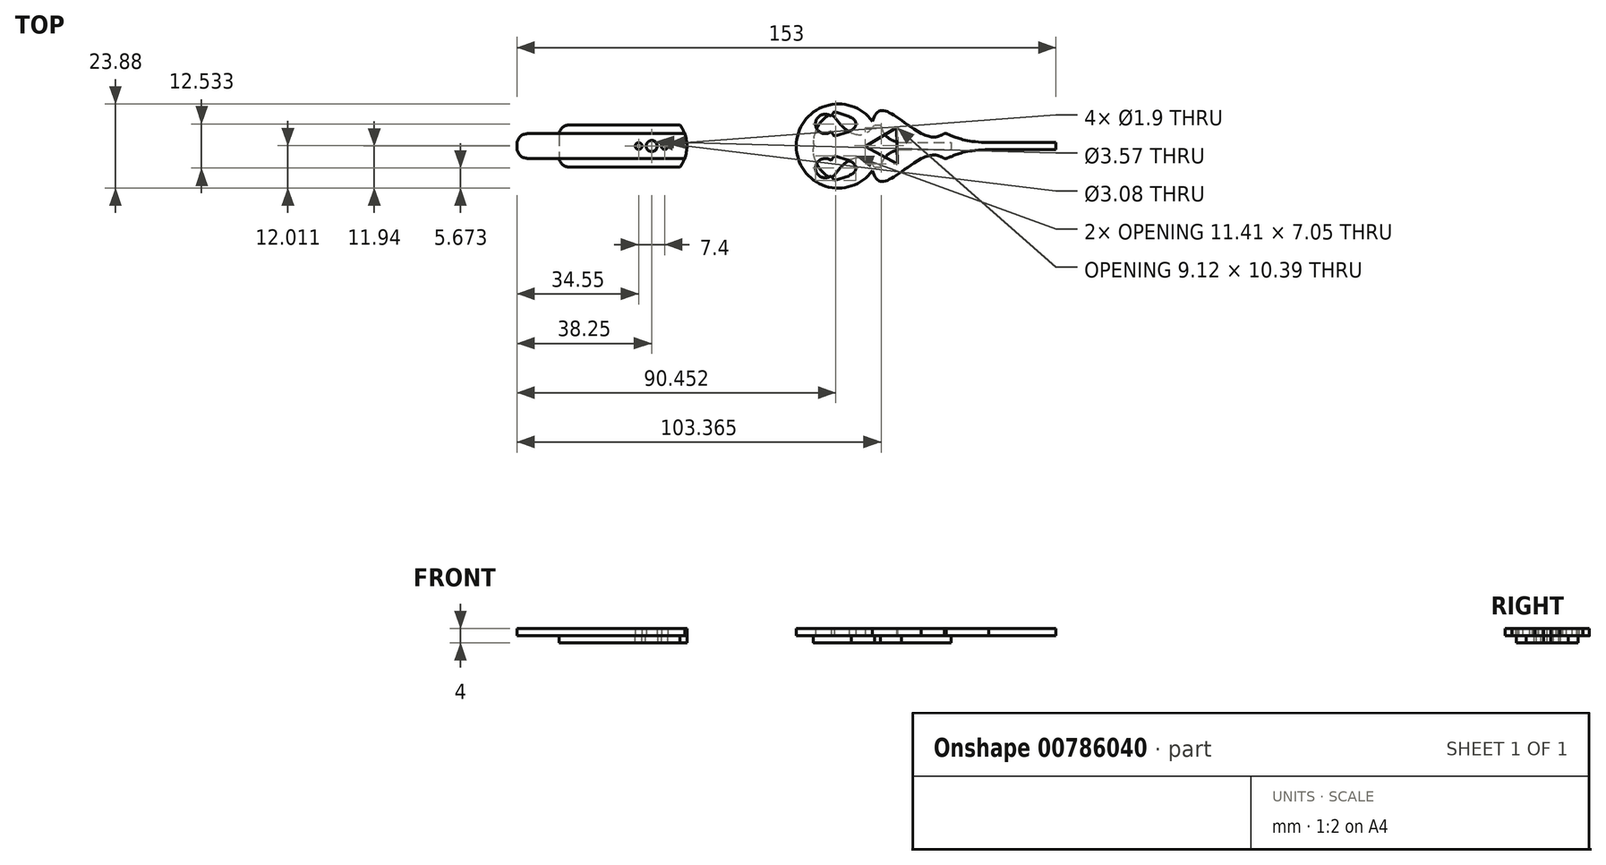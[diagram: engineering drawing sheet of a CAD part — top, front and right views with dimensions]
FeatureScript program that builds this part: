
annotation { "Feature Type Name" : "Feature", "Feature Type Description" : "" }
export const myFeature = defineFeature(function(context is Context, id is Id, definition is map)
    precondition{}
    {
        {
            var Q0;
            Q0=qCreatedBy(makeId("Top.planeOp"),FACE);
            var sketch = newSketch(context, id + "F0", { "sketchPlane" : qUnion([Q0])});
            skCircle(sketch, "E0", {"center": v(0, 0) * mm, "radius": 1.54 * mm});
            skLineSegment(sketch, "E1.bottom", {"start": v(-38.25, 3.5) * mm, "end": v(114.75, 3.5) * mm});
            skLineSegment(sketch, "E1.top", {"start": v(-38.25, -3.5) * mm, "end": v(114.75, -3.5) * mm});
            skLineSegment(sketch, "E1.left", {"start": v(-38.25, 3.5) * mm, "end": v(-38.25, -3.5) * mm});
            skLineSegment(sketch, "E1.right", {"start": v(114.75, 3.5) * mm, "end": v(114.75, -3.5) * mm});
            skCircle(sketch, "E2", {"center": v(0, 0) * mm, "radius": 10 * mm});
            skFitSpline(sketch, "E3", {"points": [v(76.5, -3.5) * mm, v(83.1, -3.5) * mm, v(95.63, -1) * mm], "startDerivative": vector(32.58, 14.52) * mm, "endDerivative": vector(48.68, 0.82) * mm});
            skFitSpline(sketch, "E4", {"points": [v(76.5, -3.5) * mm, v(64.41, -9.82) * mm, v(62.16, 0) * mm], "startDerivative": vector(-33.87, -20.38) * mm, "endDerivative": vector(3.66, 22.72) * mm});
            skLineSegment(sketch, "E5", {"start": v(0, 0) * mm, "end": v(229.5, 0) * mm, "construction": true});
            skLineSegment(sketch, "E6", {"start": v(95.63, -1) * mm, "end": v(114.75, -1) * mm});
            skFitSpline(sketch, "E7.MirrorCS", {"points": [v(76.5, 3.5) * mm, v(64.41, 9.82) * mm, v(62.16, 0) * mm], "startDerivative": vector(-33.87, 20.38) * mm, "endDerivative": vector(3.66, -22.72) * mm});
            skFitSpline(sketch, "E8.MirrorCS", {"points": [v(76.5, 3.5) * mm, v(83.1, 3.5) * mm, v(95.63, 1) * mm], "startDerivative": vector(32.58, -14.52) * mm, "endDerivative": vector(48.68, -0.82) * mm});
            skLineSegment(sketch, "E9.MirrorCS", {"start": v(95.63, 1) * mm, "end": v(114.75, 1) * mm});
            skCircle(sketch, "E10", {"center": v(52.97, 0) * mm, "radius": 11.94 * mm});
            skCircle(sketch, "E11.cCircle", {"center": v(52.97, 6.27) * mm, "radius": 3 * mm, "construction": true});
            skLineSegment(sketch, "E11.0", {"start": v(55.97, 8.45) * mm, "end": v(55.97, 4.09) * mm});
            skLineSegment(sketch, "E11.1", {"start": v(55.97, 4.09) * mm, "end": v(51.82, 2.74) * mm});
            skLineSegment(sketch, "E11.2", {"start": v(51.82, 2.74) * mm, "end": v(49.26, 6.27) * mm});
            skLineSegment(sketch, "E11.3", {"start": v(49.26, 6.27) * mm, "end": v(51.82, 9.8) * mm});
            skLineSegment(sketch, "E11.4", {"start": v(51.82, 9.8) * mm, "end": v(55.97, 8.45) * mm});
            skPoint(sketch, "E11.0.midPoint", {"position": v(55.97, 6.27) * mm});
            skCircle(sketch, "E12.MirrorC", {"center": v(52.97, -6.27) * mm, "radius": 3 * mm, "construction": true});
            skLineSegment(sketch, "E13.MirrorCS", {"start": v(51.82, -2.74) * mm, "end": v(49.26, -6.27) * mm});
            skLineSegment(sketch, "E14.MirrorCS", {"start": v(55.97, -4.09) * mm, "end": v(51.82, -2.74) * mm});
            skLineSegment(sketch, "E15.MirrorCS", {"start": v(55.97, -8.45) * mm, "end": v(55.97, -4.09) * mm});
            skLineSegment(sketch, "E16.MirrorCS", {"start": v(51.82, -9.8) * mm, "end": v(55.97, -8.45) * mm});
            skLineSegment(sketch, "E17.MirrorCS", {"start": v(49.26, -6.27) * mm, "end": v(51.82, -9.8) * mm});
            skCircle(sketch, "E18", {"center": v(49.26, 6.27) * mm, "radius": 2.76 * mm});
            skCircle(sketch, "E19.MirrorC", {"center": v(49.26, -6.27) * mm, "radius": 2.76 * mm});
            skCircle(sketch, "E20", {"center": v(55.97, 6.27) * mm, "radius": 1.94 * mm});
            skCircle(sketch, "E21.MirrorC", {"center": v(55.97, -6.27) * mm, "radius": 1.94 * mm});
            skCircle(sketch, "E22.cCircle", {"center": v(66.55, 0) * mm, "radius": 3 * mm, "construction": true});
            skLineSegment(sketch, "E22.0", {"start": v(69.43, 5.27) * mm, "end": v(69.68, -5.12) * mm});
            skLineSegment(sketch, "E22.1", {"start": v(69.68, -5.12) * mm, "end": v(60.56, -0.14) * mm});
            skLineSegment(sketch, "E22.2", {"start": v(60.56, -0.14) * mm, "end": v(69.43, 5.27) * mm});
            skPoint(sketch, "E22.0.midPoint", {"position": v(69.55, 0.07) * mm});
            skCircle(sketch, "E23", {"center": v(3.7, 0) * mm, "radius": 0.95 * mm});
            skCircle(sketch, "E24", {"center": v(-3.7, 0) * mm, "radius": 0.95 * mm});
            skSolve(sketch);
        }
        {
            var Q0;
            {var subQ0=sQuery(id+"F0.wireOp",EDGE,"E1.left");Q0=makeQuery(id+"F0.imprint","IMPRINT",FACE,{"disambiguationData":[TD([[makeQuery(id+"F0.imprint","IMPRINT",EDGE,{"derivedFrom":subQ0}),1.0]])]});}
            var Q1;
            {var subQ0=sQuery(id+"F0.wireOp",EDGE,"E2");var subQ1=sQuery(id+"F0.wireOp",EDGE,"E1.bottom");var subQ2=makeQuery(id+"F0.imprint","INTERSECT",VERTEX,{"disambiguationData":[OD(0.0)],"derivedFrom":[subQ1,subQ0]});Q1=makeQuery(id+"F0.imprint","IMPRINT",FACE,{"disambiguationData":[TD([[makeQuery(id+"F0.imprint","IMPRINT",EDGE,{"disambiguationData":[TD([[subQ2,-1.0]])],"derivedFrom":subQ1}),1.0]])]});}
            var Q2;
            {var subQ0=sQuery(id+"F0.wireOp",EDGE,"E7.MirrorCS");var subQ1=sQuery(id+"F0.wireOp",EDGE,"E1.bottom");var subQ3=makeQuery(id+"F0.imprint","INTERSECT",VERTEX,{"derivedFrom":[subQ1,subQ0]});Q2=makeQuery(id+"F0.imprint","IMPRINT",FACE,{"disambiguationData":[TD([[makeQuery(id+"F0.imprint","IMPRINT",EDGE,{"disambiguationData":[TD([[subQ3,-1.0]])],"derivedFrom":subQ1}),1.0]])]});}
            var Q3;
            {var subQ0=sQuery(id+"F0.wireOp",EDGE,"E2");var subQ1=sQuery(id+"F0.wireOp",EDGE,"E1.top");var subQ2=makeQuery(id+"F0.imprint","INTERSECT",VERTEX,{"disambiguationData":[OD(0.0)],"derivedFrom":[subQ1,subQ0]});Q3=makeQuery(id+"F0.imprint","IMPRINT",FACE,{"disambiguationData":[TD([[makeQuery(id+"F0.imprint","IMPRINT",EDGE,{"disambiguationData":[TD([[subQ2,-1.0]])],"derivedFrom":subQ1}),-1.0]])]});}
            var Q4;
            {var subQ0=sQuery(id+"F0.wireOp",EDGE,"E4");var subQ1=sQuery(id+"F0.wireOp",EDGE,"E1.top");var subQ3=makeQuery(id+"F0.imprint","INTERSECT",VERTEX,{"derivedFrom":[subQ1,subQ0]});Q4=makeQuery(id+"F0.imprint","IMPRINT",FACE,{"disambiguationData":[TD([[makeQuery(id+"F0.imprint","IMPRINT",EDGE,{"disambiguationData":[TD([[subQ3,-1.0]])],"derivedFrom":subQ1}),-1.0]])]});}
            var Q5;
            {var subQ5=sQuery(id+"F0.wireOp",EDGE,"E2");var subQ6=sQuery(id+"F0.wireOp",EDGE,"E1.bottom");var subQ7=makeQuery(id+"F0.imprint","INTERSECT",VERTEX,{"disambiguationData":[OD(1.0)],"derivedFrom":[subQ6,subQ5]});Q5=makeQuery(id+"F0.imprint","IMPRINT",FACE,{"disambiguationData":[TD([[makeQuery(id+"F0.imprint","IMPRINT",EDGE,{"disambiguationData":[TD([[subQ7,-1.0]])],"derivedFrom":subQ6}),-1.0]])]});}
            var Q6;
            Q6=makeQuery(id+"F0.imprint","IMPRINT",FACE,{"disambiguationData":[TD([[makeQuery(id+"F0.imprint","IMPRINT",EDGE,{"derivedFrom":sQuery(id+"F0.wireOp",EDGE,"E0")}),-1.0]])]});
            var Q7;
            {var subQ0=sQuery(id+"F0.wireOp",EDGE,"E10");var subQ6=sQuery(id+"F0.wireOp",EDGE,"E1.bottom");var subQ7=makeQuery(id+"F0.imprint","INTERSECT",VERTEX,{"disambiguationData":[OD(0.0)],"derivedFrom":[subQ6,subQ0]});Q7=makeQuery(id+"F0.imprint","IMPRINT",FACE,{"disambiguationData":[TD([[makeQuery(id+"F0.imprint","IMPRINT",EDGE,{"disambiguationData":[TD([[subQ7,-1.0]])],"derivedFrom":subQ6}),-1.0]])]});}
            var Q8;
            {var subQ13=sQuery(id+"F0.wireOp",EDGE,"E3");Q8=makeQuery(id+"F0.imprint","IMPRINT",FACE,{"disambiguationData":[TD([[makeQuery(id+"F0.imprint","IMPRINT",EDGE,{"derivedFrom":subQ13}),1.0]])]});}
            var Q9;
            {var subQ0=sQuery(id+"F0.wireOp",EDGE,"E7.MirrorCS");var subQ7=sQuery(id+"F0.wireOp",EDGE,"E1.bottom");var subQ8=makeQuery(id+"F0.imprint","INTERSECT",VERTEX,{"derivedFrom":[subQ7,subQ0]});Q9=makeQuery(id+"F0.imprint","IMPRINT",FACE,{"disambiguationData":[TD([[makeQuery(id+"F0.imprint","IMPRINT",EDGE,{"disambiguationData":[TD([[subQ8,-1.0]])],"derivedFrom":subQ7}),-1.0]])]});}
            var Q10;
            {var subQ0=sQuery(id+"F0.wireOp",EDGE,"E4");var subQ3=sQuery(id+"F0.wireOp",EDGE,"E10");var subQ5=makeQuery(id+"F0.imprint","INTERSECT",VERTEX,{"derivedFrom":[subQ0,subQ3]});Q10=makeQuery(id+"F0.imprint","IMPRINT",FACE,{"disambiguationData":[TD([[makeQuery(id+"F0.imprint","IMPRINT",EDGE,{"disambiguationData":[TD([[subQ5,-1.0]])],"derivedFrom":subQ3}),-1.0]])]});}
            var Q11;
            {var subQ0=sQuery(id+"F0.wireOp",EDGE,"E7.MirrorCS");var subQ3=sQuery(id+"F0.wireOp",EDGE,"E10");var subQ5=makeQuery(id+"F0.imprint","INTERSECT",VERTEX,{"derivedFrom":[subQ0,subQ3]});Q11=makeQuery(id+"F0.imprint","IMPRINT",FACE,{"disambiguationData":[TD([[makeQuery(id+"F0.imprint","IMPRINT",EDGE,{"disambiguationData":[TD([[subQ5,1.0]])],"derivedFrom":subQ3}),-1.0]])]});}
            var Q12;
            {var subQ1=sQuery(id+"F0.wireOp",EDGE,"E16.MirrorCS");Q12=makeQuery(id+"F0.imprint","IMPRINT",FACE,{"disambiguationData":[TD([[makeQuery(id+"F0.imprint","IMPRINT",EDGE,{"derivedFrom":subQ1}),-1.0]])]});}
            var Q13;
            {var subQ0=sQuery(id+"F0.wireOp",EDGE,"E11.4");Q13=makeQuery(id+"F0.imprint","IMPRINT",FACE,{"disambiguationData":[TD([[makeQuery(id+"F0.imprint","IMPRINT",EDGE,{"derivedFrom":subQ0}),1.0]])]});}
            var Q14;
            {var subQ0=sQuery(id+"F0.wireOp",EDGE,"E10");var subQ1=sQuery(id+"F0.wireOp",EDGE,"E1.top");var subQ2=makeQuery(id+"F0.imprint","INTERSECT",VERTEX,{"disambiguationData":[OD(1.0)],"derivedFrom":[subQ1,subQ0]});Q14=makeQuery(id+"F0.imprint","IMPRINT",FACE,{"disambiguationData":[TD([[makeQuery(id+"F0.imprint","IMPRINT",EDGE,{"disambiguationData":[TD([[subQ2,-1.0]])],"derivedFrom":subQ1}),1.0]])]});}
            var Q15;
            {var subQ0=sQuery(id+"F0.wireOp",EDGE,"E4");var subQ1=sQuery(id+"F0.wireOp",EDGE,"E1.top");var subQ2=makeQuery(id+"F0.imprint","INTERSECT",VERTEX,{"derivedFrom":[subQ1,subQ0]});Q15=makeQuery(id+"F0.imprint","IMPRINT",FACE,{"disambiguationData":[TD([[makeQuery(id+"F0.imprint","IMPRINT",EDGE,{"disambiguationData":[TD([[subQ2,-1.0]])],"derivedFrom":subQ1}),1.0]])]});}
            var Q16;
            {var subQ0=sQuery(id+"F0.wireOp",EDGE,"E10");var subQ1=sQuery(id+"F0.wireOp",EDGE,"E1.bottom");var subQ2=makeQuery(id+"F0.imprint","INTERSECT",VERTEX,{"disambiguationData":[OD(1.0)],"derivedFrom":[subQ1,subQ0]});Q16=makeQuery(id+"F0.imprint","IMPRINT",FACE,{"disambiguationData":[TD([[makeQuery(id+"F0.imprint","IMPRINT",EDGE,{"disambiguationData":[TD([[subQ2,-1.0]])],"derivedFrom":subQ1}),-1.0]])]});}
            var Q17;
            {var subQ4=sQuery(id+"F0.wireOp",EDGE,"E6");Q17=makeQuery(id+"F0.imprint","IMPRINT",FACE,{"disambiguationData":[TD([[makeQuery(id+"F0.imprint","IMPRINT",EDGE,{"derivedFrom":subQ4}),1.0]])]});}
            extrude(context, id + "F1", {"entities" : qUnion([Q0, Q1, Q2, Q3, Q4, Q5, Q6, Q7, Q8, Q9, Q10, Q11, Q12, Q13, Q14, Q15, Q16, Q17]), "depth" : 2 * mm, "offsetDistance" : 25 * mm});
        }
        {
            var Q0;
            Q0=qCreatedBy(makeId("Top.planeOp"),FACE);
            var sketch = newSketch(context, id + "F2", { "sketchPlane" : qUnion([Q0])});
            skCircle(sketch, "E25", {"center": v(0, 0) * mm, "radius": 1.79 * mm});
            skLineSegment(sketch, "E26.bottom", {"start": v(-26.33, 6) * mm, "end": v(85, 6) * mm});
            skLineSegment(sketch, "E26.top", {"start": v(-26.33, -6) * mm, "end": v(85, -6) * mm});
            skLineSegment(sketch, "E26.left", {"start": v(-26.33, 6) * mm, "end": v(-26.33, -6) * mm});
            skLineSegment(sketch, "E26.right", {"start": v(85, 6) * mm, "end": v(85, -6) * mm});
            skCircle(sketch, "E27", {"center": v(0, 0) * mm, "radius": 10 * mm});
            skLineSegment(sketch, "E28.right", {"start": v(85, -12.54) * mm, "end": v(85, -19.22) * mm});
            skFitSpline(sketch, "E29", {"points": [v(56.67, -3.75) * mm, v(64.42, -7.88) * mm, v(70.83, -1) * mm], "startDerivative": vector(32.58, 14.52) * mm, "endDerivative": vector(38.81, 3.07) * mm});
            skFitSpline(sketch, "E30", {"points": [v(56.67, -3.75) * mm, v(50.67, -8.78) * mm, v(46.04, 0) * mm], "startDerivative": vector(-26.59, -13.5) * mm, "endDerivative": vector(5.2, 23.3) * mm});
            skLineSegment(sketch, "E31", {"start": v(0, 0) * mm, "end": v(229.5, 0) * mm, "construction": true});
            skLineSegment(sketch, "E32", {"start": v(70.83, -1) * mm, "end": v(85, -1) * mm});
            skFitSpline(sketch, "E33.MirrorCS", {"points": [v(56.67, 3.75) * mm, v(50.67, 8.78) * mm, v(46.04, 0) * mm], "startDerivative": vector(-26.59, 13.5) * mm, "endDerivative": vector(5.2, -23.3) * mm});
            skFitSpline(sketch, "E34.MirrorCS", {"points": [v(56.67, 3.75) * mm, v(64.42, 7.88) * mm, v(70.83, 1) * mm], "startDerivative": vector(32.58, -14.52) * mm, "endDerivative": vector(38.81, -3.07) * mm});
            skLineSegment(sketch, "E35.MirrorCS", {"start": v(70.83, 1) * mm, "end": v(85, 1) * mm});
            skCircle(sketch, "E36", {"center": v(-3.7, 0) * mm, "radius": 0.95 * mm});
            skCircle(sketch, "E37", {"center": v(3.7, 0) * mm, "radius": 0.95 * mm});
            skSolve(sketch);
        }
        {
            var Q0;
            {var subQ0=sQuery(id+"F2.wireOp",EDGE,"E26.left");Q0=makeQuery(id+"F2.imprint","IMPRINT",FACE,{"disambiguationData":[TD([[makeQuery(id+"F2.imprint","IMPRINT",EDGE,{"derivedFrom":subQ0}),1.0]])]});}
            var Q1;
            {var subQ0=sQuery(id+"F2.wireOp",EDGE,"E27");var subQ1=sQuery(id+"F2.wireOp",EDGE,"E26.bottom");var subQ2=makeQuery(id+"F2.imprint","INTERSECT",VERTEX,{"disambiguationData":[OD(0.0)],"derivedFrom":[subQ1,subQ0]});Q1=makeQuery(id+"F2.imprint","IMPRINT",FACE,{"disambiguationData":[TD([[makeQuery(id+"F2.imprint","IMPRINT",EDGE,{"disambiguationData":[TD([[subQ2,-1.0]])],"derivedFrom":subQ1}),1.0]])]});}
            var Q2;
            {var subQ0=sQuery(id+"F2.wireOp",EDGE,"E27");var subQ1=sQuery(id+"F2.wireOp",EDGE,"E26.top");var subQ2=makeQuery(id+"F2.imprint","INTERSECT",VERTEX,{"disambiguationData":[OD(0.0)],"derivedFrom":[subQ1,subQ0]});Q2=makeQuery(id+"F2.imprint","IMPRINT",FACE,{"disambiguationData":[TD([[makeQuery(id+"F2.imprint","IMPRINT",EDGE,{"disambiguationData":[TD([[subQ2,-1.0]])],"derivedFrom":subQ1}),-1.0]])]});}
            var Q3;
            {var subQ0=sQuery(id+"F2.wireOp",EDGE,"E35.MirrorCS");var subQ1=sQuery(id+"F2.wireOp",EDGE,"E26.right");var subQ2=makeQuery(id+"F2.imprint","INTERSECT",VERTEX,{"derivedFrom":[subQ1,subQ0]});Q3=makeQuery(id+"F2.imprint","IMPRINT",FACE,{"disambiguationData":[TD([[makeQuery(id+"F2.imprint","IMPRINT",EDGE,{"disambiguationData":[TD([[subQ2,-1.0]])],"derivedFrom":subQ1}),1.0]])]});}
            var Q4;
            {var subQ5=sQuery(id+"F2.wireOp",EDGE,"E27");var subQ6=sQuery(id+"F2.wireOp",EDGE,"E26.bottom");var subQ7=makeQuery(id+"F2.imprint","INTERSECT",VERTEX,{"disambiguationData":[OD(1.0)],"derivedFrom":[subQ6,subQ5]});Q4=makeQuery(id+"F2.imprint","IMPRINT",FACE,{"disambiguationData":[TD([[makeQuery(id+"F2.imprint","IMPRINT",EDGE,{"disambiguationData":[TD([[subQ7,-1.0]])],"derivedFrom":subQ6}),-1.0]])]});}
            var Q5;
            Q5=makeQuery(id+"F2.imprint","IMPRINT",FACE,{"disambiguationData":[TD([[makeQuery(id+"F2.imprint","IMPRINT",EDGE,{"derivedFrom":sQuery(id+"F2.wireOp",EDGE,"E25")}),-1.0]])]});
            var Q6;
            {var subQ0=sQuery(id+"F2.wireOp",EDGE,"E32");Q6=makeQuery(id+"F2.imprint","IMPRINT",FACE,{"disambiguationData":[TD([[makeQuery(id+"F2.imprint","IMPRINT",EDGE,{"derivedFrom":subQ0}),1.0]])]});}
            var Q7;
            {var subQ0=sQuery(id+"F2.wireOp",EDGE,"E29");var subQ1=sQuery(id+"F2.wireOp",EDGE,"E26.top");var subQ2=makeQuery(id+"F2.imprint","INTERSECT",VERTEX,{"disambiguationData":[OD(0.0)],"derivedFrom":[subQ1,subQ0]});Q7=makeQuery(id+"F2.imprint","IMPRINT",FACE,{"disambiguationData":[TD([[makeQuery(id+"F2.imprint","IMPRINT",EDGE,{"disambiguationData":[TD([[subQ2,-1.0]])],"derivedFrom":subQ1}),-1.0]])]});}
            var Q8;
            {var subQ0=sQuery(id+"F2.wireOp",EDGE,"E34.MirrorCS");var subQ1=sQuery(id+"F2.wireOp",EDGE,"E26.bottom");var subQ2=makeQuery(id+"F2.imprint","INTERSECT",VERTEX,{"disambiguationData":[OD(0.0)],"derivedFrom":[subQ1,subQ0]});Q8=makeQuery(id+"F2.imprint","IMPRINT",FACE,{"disambiguationData":[TD([[makeQuery(id+"F2.imprint","IMPRINT",EDGE,{"disambiguationData":[TD([[subQ2,-1.0]])],"derivedFrom":subQ1}),1.0]])]});}
            var Q9;
            {var subQ0=sQuery(id+"F2.wireOp",EDGE,"E33.MirrorCS");var subQ1=sQuery(id+"F2.wireOp",EDGE,"E26.bottom");var subQ2=makeQuery(id+"F2.imprint","INTERSECT",VERTEX,{"disambiguationData":[OD(0.0)],"derivedFrom":[subQ1,subQ0]});Q9=makeQuery(id+"F2.imprint","IMPRINT",FACE,{"disambiguationData":[TD([[makeQuery(id+"F2.imprint","IMPRINT",EDGE,{"disambiguationData":[TD([[subQ2,-1.0]])],"derivedFrom":subQ1}),1.0]])]});}
            var Q10;
            {var subQ0=sQuery(id+"F2.wireOp",EDGE,"E30");var subQ1=sQuery(id+"F2.wireOp",EDGE,"E26.top");var subQ2=makeQuery(id+"F2.imprint","INTERSECT",VERTEX,{"disambiguationData":[OD(0.0)],"derivedFrom":[subQ1,subQ0]});Q10=makeQuery(id+"F2.imprint","IMPRINT",FACE,{"disambiguationData":[TD([[makeQuery(id+"F2.imprint","IMPRINT",EDGE,{"disambiguationData":[TD([[subQ2,-1.0]])],"derivedFrom":subQ1}),-1.0]])]});}
            extrude(context, id + "F3", {"entities" : qUnion([Q0, Q1, Q2, Q3, Q4, Q5, Q6, Q7, Q8, Q9, Q10]), "oppositeDirection" : true, "depth" : 2 * mm});
        }
        {
            var Q0;
            Q0=makeQuery(id+"F3.opExtrude","SWEPT_EDGE",EDGE,{"disambiguationData":[OSD([sQuery(id+"F2.wireOp",EDGE,"E26.bottom"),sQuery(id+"F2.wireOp",EDGE,"E26.left")])]});
            var Q1;
            Q1=makeQuery(id+"F3.opExtrude","SWEPT_EDGE",EDGE,{"disambiguationData":[OSD([sQuery(id+"F2.wireOp",EDGE,"E26.top"),sQuery(id+"F2.wireOp",EDGE,"E26.left")])]});
            var Q2;
            Q2=makeQuery(id+"F1.opExtrude","SWEPT_EDGE",EDGE,{"disambiguationData":[OSD([sQuery(id+"F0.wireOp",EDGE,"E1.bottom"),sQuery(id+"F0.wireOp",EDGE,"E1.left")])]});
            var Q3;
            Q3=makeQuery(id+"F1.opExtrude","SWEPT_EDGE",EDGE,{"disambiguationData":[OSD([sQuery(id+"F0.wireOp",EDGE,"E1.top"),sQuery(id+"F0.wireOp",EDGE,"E1.left")])]});
            fillet(context, id + "F4", {"entities" : qUnion([Q0, Q1, Q2, Q3]), "radius" : 3 * mm, "tangentPropagation" : true, "allowEdgeOverflow" : false});
        }
    });
